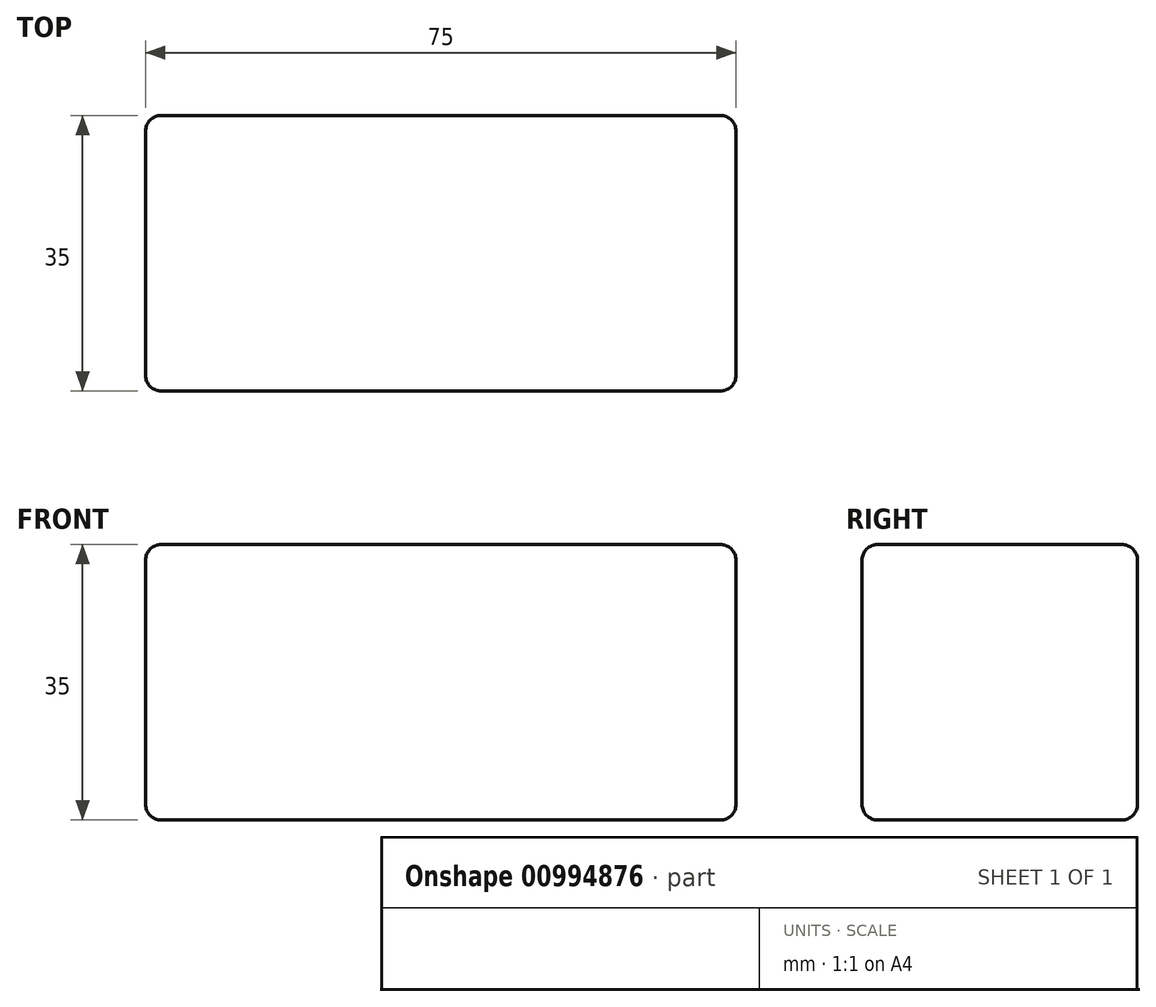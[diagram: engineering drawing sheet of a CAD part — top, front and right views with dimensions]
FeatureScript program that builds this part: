
annotation { "Feature Type Name" : "Feature", "Feature Type Description" : "" }
export const myFeature = defineFeature(function(context is Context, id is Id, definition is map)
    precondition{}
    {
        {
            var Q0;
            Q0=qCreatedBy(makeId("Top.planeOp"),FACE);
            var sketch = newSketch(context, id + "F0", { "sketchPlane" : qUnion([Q0])});
            skLineSegment(sketch, "E0.bottom", {"start": v(37.5, -17.5) * mm, "end": v(-37.5, -17.5) * mm});
            skLineSegment(sketch, "E0.top", {"start": v(37.5, 17.5) * mm, "end": v(-37.5, 17.5) * mm});
            skLineSegment(sketch, "E0.left", {"start": v(37.5, -17.5) * mm, "end": v(37.5, 17.5) * mm});
            skLineSegment(sketch, "E0.right", {"start": v(-37.5, -17.5) * mm, "end": v(-37.5, 17.5) * mm});
            skPoint(sketch, "E0.middle", {"position": v(0, 0) * mm});
            skSolve(sketch);
        }
        {
            var Q0;
            Q0=qSketchRegion(id+"F0",true);
            extrude(context, id + "F1", {"entities" : qUnion([Q0]), "depth" : 35 * mm, "offsetDistance" : 25 * mm});
        }
        {
            var Q0;
            Q0=makeQuery(id+"F1.opExtrude","CAP_EDGE",EDGE,{"disambiguationData":[OSD([sQuery(id+"F0.wireOp",EDGE,"E0.bottom")])],"isStart":false});
            var Q1;
            Q1=makeQuery(id+"F1.opExtrude","SWEPT_EDGE",EDGE,{"disambiguationData":[OSD([sQuery(id+"F0.wireOp",EDGE,"E0.bottom"),sQuery(id+"F0.wireOp",EDGE,"E0.left")])]});
            var Q2;
            Q2=makeQuery(id+"F1.opExtrude","CAP_EDGE",EDGE,{"disambiguationData":[OSD([sQuery(id+"F0.wireOp",EDGE,"E0.left")])],"isStart":false});
            var Q3;
            Q3=makeQuery(id+"F1.opExtrude","SWEPT_EDGE",EDGE,{"disambiguationData":[OSD([sQuery(id+"F0.wireOp",EDGE,"E0.top"),sQuery(id+"F0.wireOp",EDGE,"E0.left")])]});
            var Q4;
            Q4=makeQuery(id+"F1.opExtrude","CAP_EDGE",EDGE,{"disambiguationData":[OSD([sQuery(id+"F0.wireOp",EDGE,"E0.left")])],"isStart":true});
            var Q5;
            Q5=makeQuery(id+"F1.opExtrude","CAP_EDGE",EDGE,{"disambiguationData":[OSD([sQuery(id+"F0.wireOp",EDGE,"E0.bottom")])],"isStart":true});
            var Q6;
            Q6=makeQuery(id+"F1.opExtrude","SWEPT_EDGE",EDGE,{"disambiguationData":[OSD([sQuery(id+"F0.wireOp",EDGE,"E0.bottom"),sQuery(id+"F0.wireOp",EDGE,"E0.right")])]});
            var Q7;
            Q7=makeQuery(id+"F1.opExtrude","CAP_EDGE",EDGE,{"disambiguationData":[OSD([sQuery(id+"F0.wireOp",EDGE,"E0.top")])],"isStart":true});
            var Q8;
            Q8=makeQuery(id+"F1.opExtrude","CAP_EDGE",EDGE,{"disambiguationData":[OSD([sQuery(id+"F0.wireOp",EDGE,"E0.right")])],"isStart":true});
            var Q9;
            Q9=makeQuery(id+"F1.opExtrude","SWEPT_EDGE",EDGE,{"disambiguationData":[OSD([sQuery(id+"F0.wireOp",EDGE,"E0.top"),sQuery(id+"F0.wireOp",EDGE,"E0.right")])]});
            var Q10;
            Q10=makeQuery(id+"F1.opExtrude","CAP_EDGE",EDGE,{"disambiguationData":[OSD([sQuery(id+"F0.wireOp",EDGE,"E0.right")])],"isStart":false});
            var Q11;
            Q11=makeQuery(id+"F1.opExtrude","CAP_EDGE",EDGE,{"disambiguationData":[OSD([sQuery(id+"F0.wireOp",EDGE,"E0.top")])],"isStart":false});
            fillet(context, id + "F2", {"entities" : qUnion([Q0, Q1, Q2, Q3, Q4, Q5, Q6, Q7, Q8, Q9, Q10, Q11]), "radius" : 2 * mm, "tangentPropagation" : true, "allowEdgeOverflow" : false});
        }
    });
